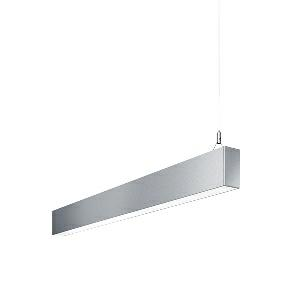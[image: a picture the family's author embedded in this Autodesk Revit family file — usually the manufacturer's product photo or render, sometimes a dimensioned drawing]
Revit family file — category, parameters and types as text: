
# Revit family: idoo_line_-_ilp_4000_840_d_end_00805701_6922
name_source: partatom
category: Lighting Fixtures
units: mm (PartAtom-declared; Revit-internal decimal feet)

## family parameters
Cut with Voids When Loaded = No
Host = Face
Light Source = No
Part Type = Normal
Room Calculation Point = No
Round Connector Dimension = Use Diameter
Shared = No

## types (1)
- IDOO.line - ILP 4000/840/D END (1 x LED, 3950 lm, 4000K)
    Apparent Load = 29 VA
    Approval mark = CE
    CIE Flux Codes = 66 91 98 40 100
    Color Rendering = 80-89
    Color Temperature = 4000K
    Control Gear = Electronic ballast
    Default Elevation = 1800 mm
    Description = ILP 4000/840/D|Suspended luminaire|light source: LED|connected load: 220-240 V, 50/60 Hz|Power consumption: approx. 29 W|standby: approx. 0,15|luminous flux: 3950 lm|luminous efficacy: 136 lm/W|light distribution: Direct/indirect|direct ratio: approx. 40 %|colour temperature: Cold white, ca. 4000 K|color rendering index (CRI): >= 80|chromaticity tolerance:  3 SDCM|System of protection: IP 40|technology: Continuously dimmable|luminaire body|material: Sectional aluminium|colour: Silver|lamp cover: Acrylic (PMMA), Clear|mains lead: 1,0 m With free stranded wires|Fastening: Steel cable 0.3 - 0.7 m|glare control: Prism aperture|luminance(L65): <= 2700 cd/m|unified glare rating(4H 8H): <=  16|special features: DALI Load 1x, TouchDIM - dimming via standard switch, Through-wired, up to 18 m on one mains connection, Flicker-free, Suitable as emergency lighting, Mechanical and electrical connection of the individual modules without tools|
    Frequency = 50 Hz
    Height = 110 mm
    Lamp = 1 x LED
    Lamp Light Flux = 3950 lm
    Lamp count = 1
    Length = 1408 mm
    Luminous efficacy = 136 lm/W
    Manufacturer = Waldmann
    ModVariant = No
    Model = 00805701
    Mounting Place = Ceiling
    Mounting Type = Pendant
    Number of Poles = 1
    OnlyDefault = Yes
    Power Factor = 1
    Product Name = IDOO.line - ILP 4000/840/D END
    Product group = Suspended luminaire
    ProductGroupID = 9
    Protection Class = Protection class I
    Protection Degree = IP 40
    RLX_Detail_Level = 1
    RLX_Emergency_Light_Flux = 0 lm
    RLX_Emergency_Type = 0
    RLX_Emergency_Type_DB = No
    RlxData = <blob elided: 20605 chars, md5=1649f2de>
    Socket = socket
    Standby Power = 0 W
    System Light Flux = 3950 lm
    System Power = 29 W
    Type Comments = Product without accessories
    Type Image = 113312000-00692600.jpg
    URL = http://relux.com
    VarID = ---
    Voltage = 230 V
    Voltage Range = 220-240 V
    Weight = 0.00 kg
    Width = 60 mm  [stored 0.19685 ft]

note: [stored X ft] marks values corroborated as IEEE doubles in the binary element streams (Revit-internal decimal feet)

## geometry (parser evidence)
native form markers: Blend x4, Sweep x14
no freeform markers — native parametric forms only
